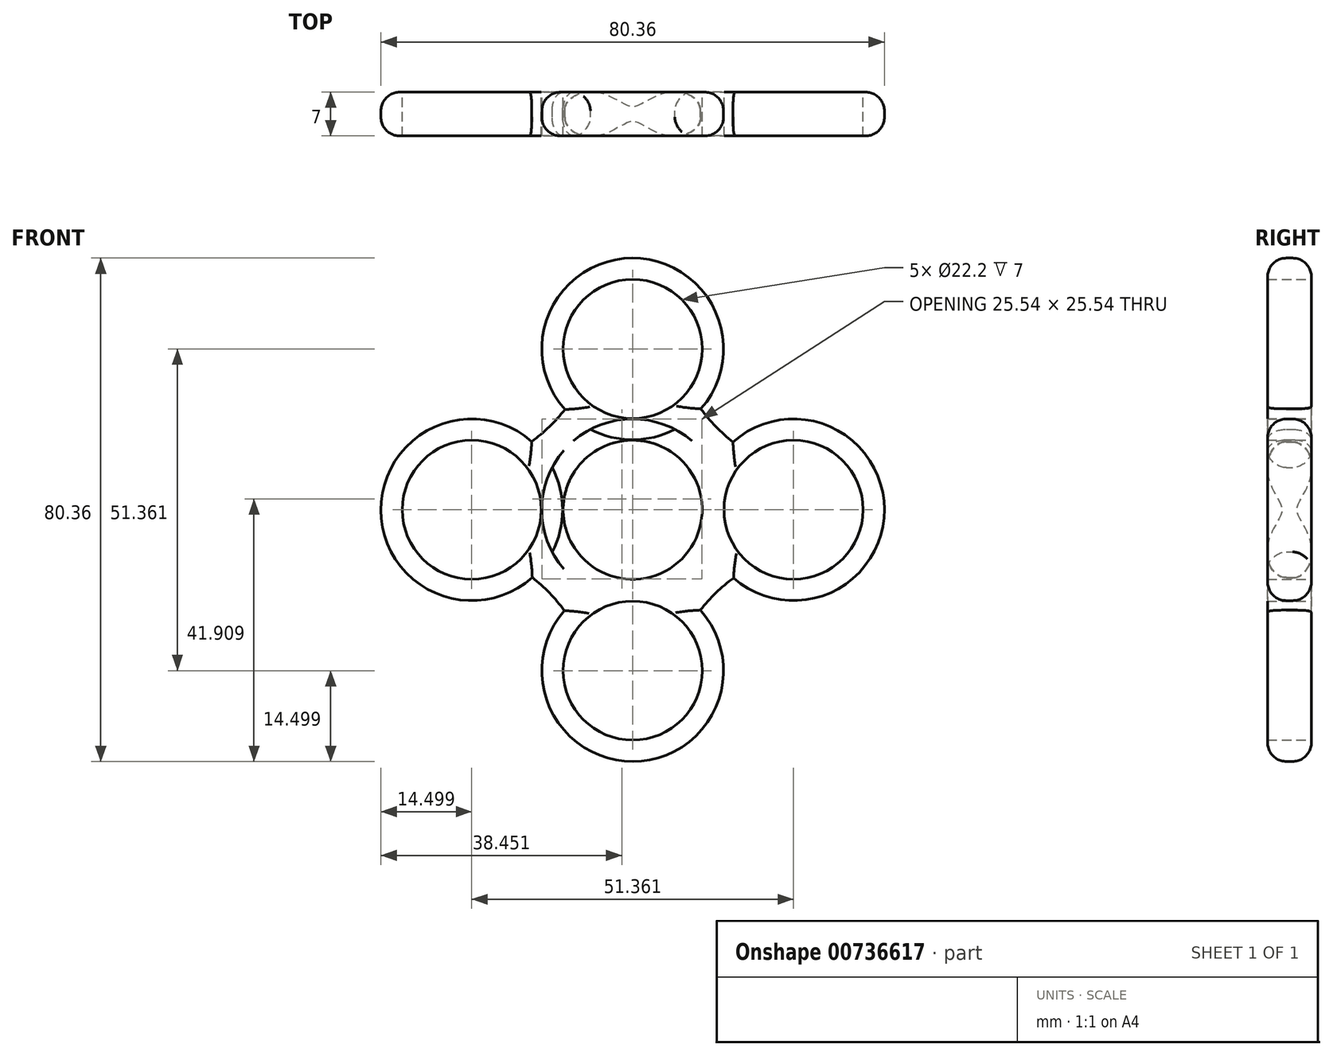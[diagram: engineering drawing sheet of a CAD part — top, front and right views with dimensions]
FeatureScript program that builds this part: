
annotation { "Feature Type Name" : "Feature", "Feature Type Description" : "" }
export const myFeature = defineFeature(function(context is Context, id is Id, definition is map)
    precondition{}
    {
        {
            var Q0;
            Q0=qCreatedBy(makeId("Front.planeOp"),FACE);
            var sketch = newSketch(context, id + "F0", { "sketchPlane" : qUnion([Q0])});
            skCircle(sketch, "E0", {"center": v(0, 0) * mm, "radius": 11.1 * mm});
            skCircle(sketch, "E1", {"center": v(0, 0) * mm, "radius": 14.5 * mm});
            skCircle(sketch, "E2", {"center": v(0, 25.68) * mm, "radius": 14.5 * mm});
            skCircle(sketch, "E3", {"center": v(0, 25.68) * mm, "radius": 11.1 * mm});
            skCircle(sketch, "E4.1.0", {"center": v(-25.68, 0) * mm, "radius": 11.1 * mm});
            skCircle(sketch, "E4.1.3", {"center": v(-25.68, 0) * mm, "radius": 14.5 * mm});
            skCircle(sketch, "E4.2.0", {"center": v(0, -25.68) * mm, "radius": 11.1 * mm});
            skCircle(sketch, "E4.2.3", {"center": v(0, -25.68) * mm, "radius": 14.5 * mm});
            skCircle(sketch, "E4.3.0", {"center": v(25.68, 0) * mm, "radius": 11.1 * mm});
            skCircle(sketch, "E4.3.3", {"center": v(25.68, 0) * mm, "radius": 14.5 * mm});
            skArc(sketch, "E5", {"start": v(10.9, 16.1) * mm, "mid": v(13.28, 13.29) * mm, "end": v(16.02, 10.81) * mm});
            skArc(sketch, "E6.1.0", {"start": v(-16.1, 10.9) * mm, "mid": v(-13.29, 13.28) * mm, "end": v(-10.81, 16.02) * mm});
            skArc(sketch, "E6.2.0", {"start": v(-10.9, -16.1) * mm, "mid": v(-13.28, -13.29) * mm, "end": v(-16.02, -10.81) * mm});
            skArc(sketch, "E6.3.0", {"start": v(16.1, -10.9) * mm, "mid": v(13.29, -13.28) * mm, "end": v(10.81, -16.02) * mm});
            skSolve(sketch);
        }
        {
            var Q0;
            Q0 = qSketchRegion(id + "F0", true);
            var Q1;
            Q1=makeQuery(id+"F0.imprint","IMPRINT",FACE,{"disambiguationData":[TD([[makeQuery(id+"F0.imprint","IMPRINT",EDGE,{"derivedFrom":sQuery(id+"F0.wireOp",EDGE,"E0")}),-1.0]])]});
            var Q2;
            {var subQ0=sQuery(id+"F0.wireOp",EDGE,"E1");var subQ1=sQuery(id+"F0.wireOp",EDGE,"E4.1.3");var subQ2=makeQuery(id+"F0.imprint","INTERSECT",VERTEX,{"disambiguationData":[OD(0.0)],"derivedFrom":[subQ1,subQ0]});Q2=makeQuery(id+"F0.imprint","IMPRINT",FACE,{"disambiguationData":[TD([[makeQuery(id+"F0.imprint","IMPRINT",EDGE,{"disambiguationData":[TD([[subQ2,-1.0]])],"derivedFrom":subQ1}),1.0]])]});}
            var Q3;
            {var subQ0=sQuery(id+"F0.wireOp",EDGE,"E1");var subQ1=sQuery(id+"F0.wireOp",EDGE,"E4.2.3");var subQ2=makeQuery(id+"F0.imprint","INTERSECT",VERTEX,{"disambiguationData":[OD(0.0)],"derivedFrom":[subQ1,subQ0]});Q3=makeQuery(id+"F0.imprint","IMPRINT",FACE,{"disambiguationData":[TD([[makeQuery(id+"F0.imprint","IMPRINT",EDGE,{"disambiguationData":[TD([[subQ2,-1.0]])],"derivedFrom":subQ1}),1.0]])]});}
            var Q4;
            {var subQ0=sQuery(id+"F0.wireOp",EDGE,"E4.3.3");var subQ1=sQuery(id+"F0.wireOp",EDGE,"E1");var subQ2=makeQuery(id+"F0.imprint","INTERSECT",VERTEX,{"disambiguationData":[OD(0.0)],"derivedFrom":[subQ1,subQ0]});Q4=makeQuery(id+"F0.imprint","IMPRINT",FACE,{"disambiguationData":[TD([[makeQuery(id+"F0.imprint","IMPRINT",EDGE,{"disambiguationData":[TD([[subQ2,-1.0]])],"derivedFrom":subQ1}),1.0]])]});}
            var Q5;
            {var subQ0=sQuery(id+"F0.wireOp",EDGE,"E1");var subQ1=sQuery(id+"F0.wireOp",EDGE,"E2");var subQ2=makeQuery(id+"F0.imprint","INTERSECT",VERTEX,{"disambiguationData":[OD(0.0)],"derivedFrom":[subQ1,subQ0]});Q5=makeQuery(id+"F0.imprint","IMPRINT",FACE,{"disambiguationData":[TD([[makeQuery(id+"F0.imprint","IMPRINT",EDGE,{"disambiguationData":[TD([[subQ2,-1.0]])],"derivedFrom":subQ1}),1.0]])]});}
            extrude(context, id + "F1", {"entities" : qUnion([Q0, Q1, Q2, Q3, Q4, Q5]), "depth" : 7 * mm, "offsetDistance" : 25 * mm});
        }
        {
            var Q0;
            Q0=makeQuery(id+"F1.opExtrude","CAP_EDGE",EDGE,{"disambiguationData":[OSD([sQuery(id+"F0.wireOp",EDGE,"E2")])],"isStart":false});
            var Q1;
            Q1=makeQuery(id+"F1.opExtrude","CAP_EDGE",EDGE,{"disambiguationData":[OSD([sQuery(id+"F0.wireOp",EDGE,"E6.1.0")])],"isStart":false});
            var Q2;
            Q2=makeQuery(id+"F1.opExtrude","CAP_EDGE",EDGE,{"disambiguationData":[OSD([sQuery(id+"F0.wireOp",EDGE,"E4.1.3")])],"isStart":false});
            var Q3;
            Q3=makeQuery(id+"F1.opExtrude","CAP_EDGE",EDGE,{"disambiguationData":[OSD([sQuery(id+"F0.wireOp",EDGE,"E6.2.0")])],"isStart":false});
            var Q4;
            Q4=makeQuery(id+"F1.opExtrude","CAP_EDGE",EDGE,{"disambiguationData":[OSD([sQuery(id+"F0.wireOp",EDGE,"E4.2.3")])],"isStart":false});
            var Q5;
            Q5=makeQuery(id+"F1.opExtrude","CAP_EDGE",EDGE,{"disambiguationData":[OSD([sQuery(id+"F0.wireOp",EDGE,"E6.3.0")])],"isStart":false});
            var Q6;
            Q6=makeQuery(id+"F1.opExtrude","CAP_EDGE",EDGE,{"disambiguationData":[OSD([sQuery(id+"F0.wireOp",EDGE,"E4.3.3")])],"isStart":false});
            var Q7;
            Q7=makeQuery(id+"F1.opExtrude","CAP_EDGE",EDGE,{"disambiguationData":[OSD([sQuery(id+"F0.wireOp",EDGE,"E5")])],"isStart":false});
            var Q8;
            Q8=makeQuery(id+"F1.opExtrude","CAP_EDGE",EDGE,{"disambiguationData":[OSD([sQuery(id+"F0.wireOp",EDGE,"E4.1.3")])],"isStart":true});
            var Q9;
            Q9=makeQuery(id+"F1.opExtrude","CAP_EDGE",EDGE,{"disambiguationData":[OSD([sQuery(id+"F0.wireOp",EDGE,"E6.1.0")])],"isStart":true});
            var Q10;
            Q10=makeQuery(id+"F1.opExtrude","CAP_EDGE",EDGE,{"disambiguationData":[OSD([sQuery(id+"F0.wireOp",EDGE,"E2")])],"isStart":true});
            var Q11;
            Q11=makeQuery(id+"F1.opExtrude","CAP_EDGE",EDGE,{"disambiguationData":[OSD([sQuery(id+"F0.wireOp",EDGE,"E5")])],"isStart":true});
            var Q12;
            Q12=makeQuery(id+"F1.opExtrude","CAP_EDGE",EDGE,{"disambiguationData":[OSD([sQuery(id+"F0.wireOp",EDGE,"E6.3.0")])],"isStart":true});
            var Q13;
            Q13=makeQuery(id+"F1.opExtrude","CAP_EDGE",EDGE,{"disambiguationData":[OSD([sQuery(id+"F0.wireOp",EDGE,"E4.2.3")])],"isStart":true});
            var Q14;
            Q14=makeQuery(id+"F1.opExtrude","CAP_EDGE",EDGE,{"disambiguationData":[OSD([sQuery(id+"F0.wireOp",EDGE,"E6.2.0")])],"isStart":true});
            var Q15;
            Q15=makeQuery(id+"F1.opExtrude","CAP_EDGE",EDGE,{"disambiguationData":[OSD([sQuery(id+"F0.wireOp",EDGE,"E4.3.3")])],"isStart":true});
            fillet(context, id + "F2", {"entities" : qUnion([Q0, Q1, Q2, Q3, Q4, Q5, Q6, Q7, Q8, Q9, Q10, Q11, Q12, Q13, Q14, Q15]), "radius" : 3 * mm, "tangentPropagation" : true, "allowEdgeOverflow" : false});
        }
    });
